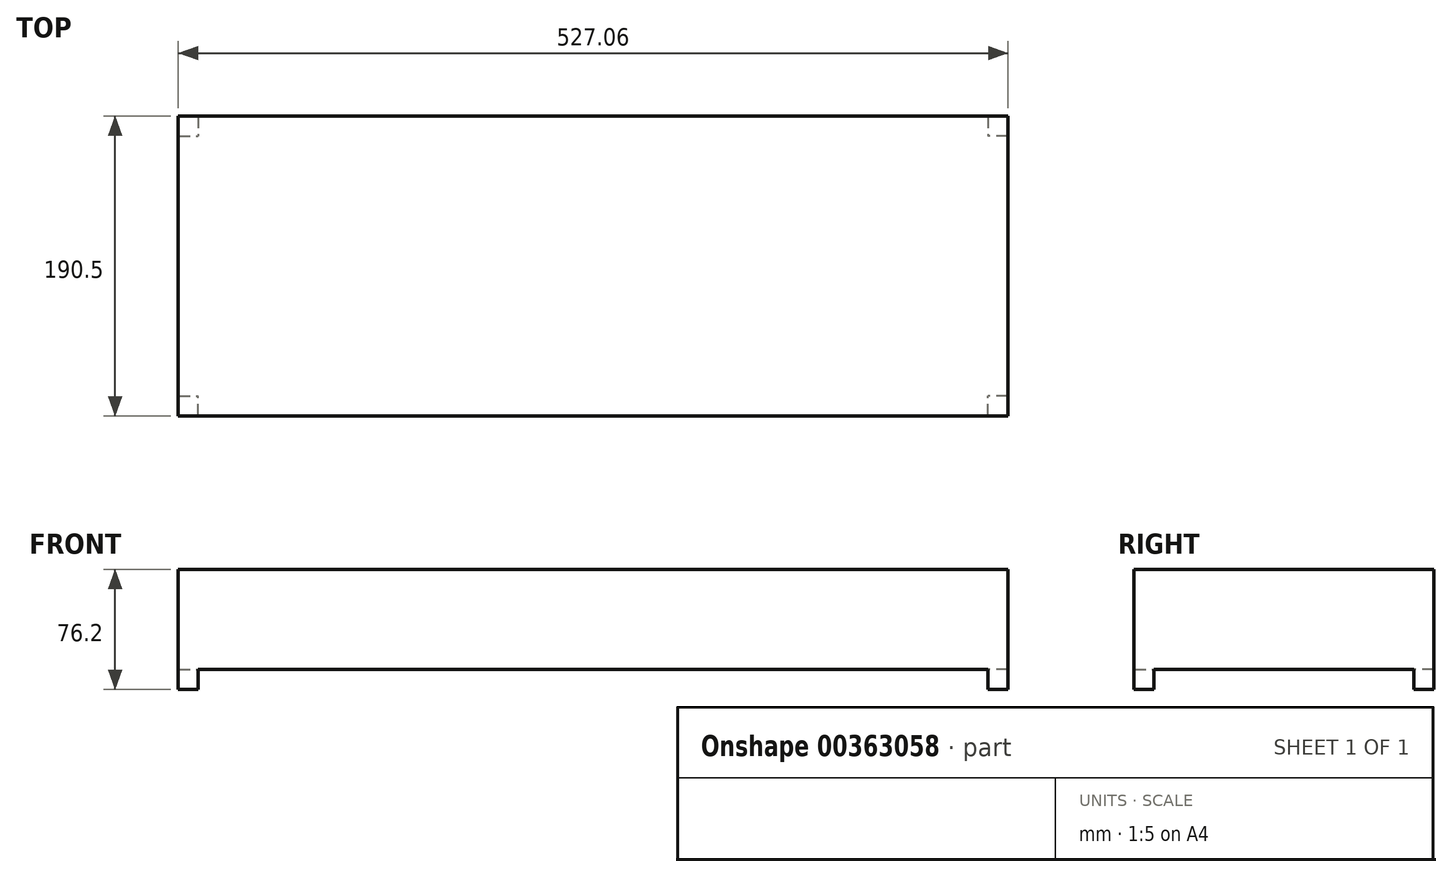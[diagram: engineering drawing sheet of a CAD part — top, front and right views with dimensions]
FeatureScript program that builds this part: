
annotation { "Feature Type Name" : "Feature", "Feature Type Description" : "" }
export const myFeature = defineFeature(function(context is Context, id is Id, definition is map)
    precondition{}
    {
        {
            var Q0;
            Q0=qCreatedBy(makeId("Top.planeOp"),FACE);
            var sketch = newSketch(context, id + "F0", { "sketchPlane" : qUnion([Q0])});
            skLineSegment(sketch, "E0.bottom", {"start": v(-263.52, 95.25) * mm, "end": v(263.53, 95.25) * mm});
            skLineSegment(sketch, "E0.top", {"start": v(-263.53, -95.25) * mm, "end": v(263.52, -95.25) * mm});
            skLineSegment(sketch, "E0.left", {"start": v(-263.53, 95.25) * mm, "end": v(-263.53, -95.25) * mm});
            skLineSegment(sketch, "E0.right", {"start": v(263.53, 95.25) * mm, "end": v(263.52, -95.25) * mm});
            skPoint(sketch, "E0.middle", {"position": v(0, 0) * mm});
            skSolve(sketch);
        }
        {
            var Q0;
            Q0 = qSketchRegion(id + "F0", true);
            extrude(context, id + "F1", {"entities" : qUnion([Q0]), "endBound" : BoundingType.SYMMETRIC, "depth" : 76.2 * mm, "offsetDistance" : 25.4 * mm});
        }
        {
            var Q0;
            Q0=makeQuery(id+"F1.opExtrude","CAP_FACE",FACE,{"disambiguationData":[OSD([sQuery(id+"F0.wireOp",EDGE,"E0.bottom"),sQuery(id+"F0.wireOp",EDGE,"E0.top"),sQuery(id+"F0.wireOp",EDGE,"E0.left"),sQuery(id+"F0.wireOp",EDGE,"E0.right")])],"isStart":true});
            var sketch = newSketch(context, id + "F2", { "sketchPlane" : qUnion([Q0])});
            skLineSegment(sketch, "E1.bottom", {"start": v(-263.53, 95.25) * mm, "end": v(-250.83, 95.25) * mm});
            skLineSegment(sketch, "E1.top", {"start": v(-263.53, 82.55) * mm, "end": v(-250.83, 82.55) * mm});
            skLineSegment(sketch, "E1.left", {"start": v(-263.53, 95.25) * mm, "end": v(-263.53, 82.55) * mm});
            skLineSegment(sketch, "E1.right", {"start": v(-250.83, 95.25) * mm, "end": v(-250.83, 82.55) * mm});
            skLineSegment(sketch, "E2.bottom", {"start": v(-263.52, -95.25) * mm, "end": v(-250.83, -95.25) * mm});
            skLineSegment(sketch, "E2.top", {"start": v(-263.53, -82.55) * mm, "end": v(-250.83, -82.55) * mm});
            skLineSegment(sketch, "E2.left", {"start": v(-263.52, -95.25) * mm, "end": v(-263.52, -82.55) * mm});
            skLineSegment(sketch, "E2.right", {"start": v(-250.83, -95.25) * mm, "end": v(-250.83, -82.55) * mm});
            skLineSegment(sketch, "E3.bottom", {"start": v(263.53, -95.25) * mm, "end": v(250.83, -95.25) * mm});
            skLineSegment(sketch, "E3.top", {"start": v(263.53, -82.55) * mm, "end": v(250.83, -82.55) * mm});
            skLineSegment(sketch, "E3.left", {"start": v(263.53, -95.25) * mm, "end": v(263.53, -82.55) * mm});
            skLineSegment(sketch, "E3.right", {"start": v(250.83, -95.25) * mm, "end": v(250.83, -82.55) * mm});
            skLineSegment(sketch, "E4.bottom", {"start": v(263.52, 95.25) * mm, "end": v(250.83, 95.25) * mm});
            skLineSegment(sketch, "E4.top", {"start": v(263.53, 82.55) * mm, "end": v(250.83, 82.55) * mm});
            skLineSegment(sketch, "E4.left", {"start": v(263.52, 95.25) * mm, "end": v(263.52, 82.55) * mm});
            skLineSegment(sketch, "E4.right", {"start": v(250.83, 95.25) * mm, "end": v(250.83, 82.55) * mm});
            skSolve(sketch);
        }
        {
            var Q0;
            {var subQ6=sQuery(id+"F2.wireOp",EDGE,"E1.top");Q0=makeQuery(id+"F2.imprint","IMPRINT",FACE,{"disambiguationData":[TD([[makeQuery(id+"F2.imprint","IMPRINT",EDGE,{"derivedFrom":subQ6}),-1.0]])]});}
            extrude(context, id + "F3", {"entities" : qUnion([Q0]), "operationType" : NewBodyOperationType.REMOVE, "oppositeDirection" : true, "depth" : 12.7 * mm, "offsetDistance" : 25.4 * mm});
        }
    });
